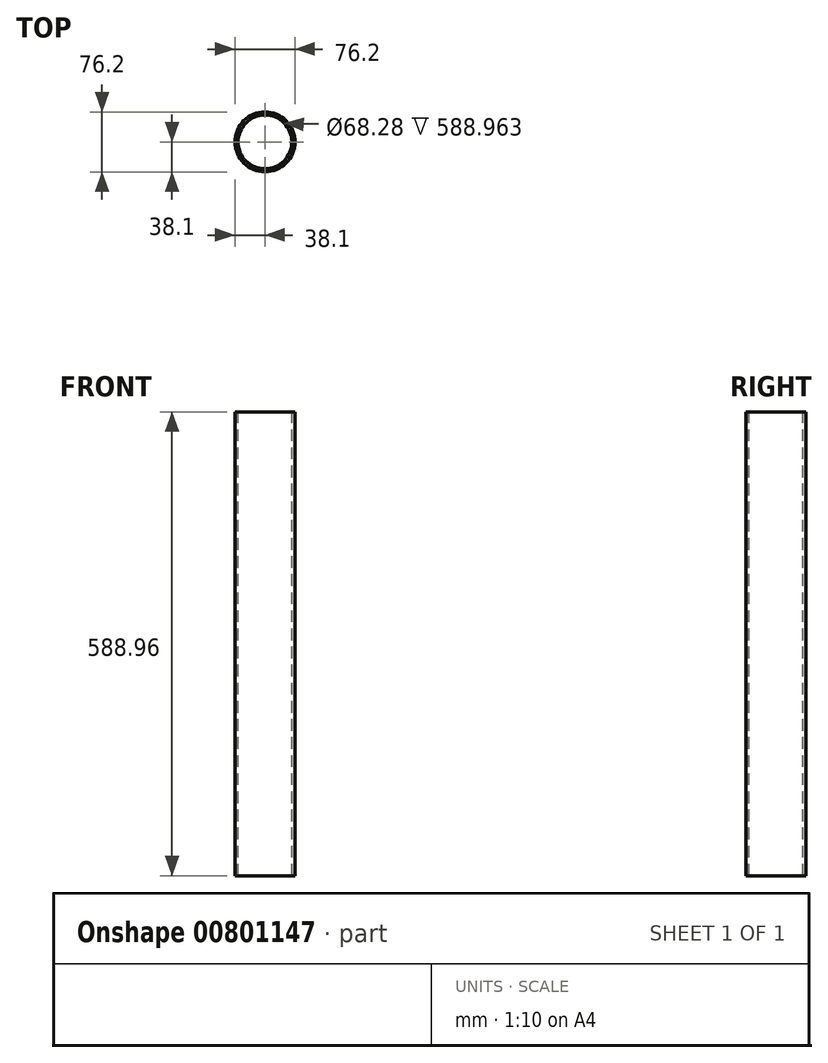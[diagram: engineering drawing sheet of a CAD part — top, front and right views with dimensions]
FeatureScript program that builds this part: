
annotation { "Feature Type Name" : "Feature", "Feature Type Description" : "" }
export const myFeature = defineFeature(function(context is Context, id is Id, definition is map)
    precondition{}
    {
        {
            var Q0;
            Q0=qCreatedBy(makeId("Top.planeOp"),FACE);
            var sketch = newSketch(context, id + "F0", { "sketchPlane" : qUnion([Q0])});
            skCircle(sketch, "E0", {"center": v(0, 0) * mm, "radius": 38.1 * mm});
            skCircle(sketch, "E1", {"center": v(0, 0) * mm, "radius": 34.14 * mm});
            skSolve(sketch);
        }
        {
            var Q0;
            Q0=makeQuery(id+"F0.imprint","IMPRINT",FACE,{"disambiguationData":[TD([[makeQuery(id+"F0.imprint","IMPRINT",EDGE,{"derivedFrom":sQuery(id+"F0.wireOp",EDGE,"E0")}),1.0]])]});
            extrude(context, id + "F1", {"entities" : qUnion([Q0]), "oppositeDirection" : true, "depth" : 588.96 * mm, "offsetDistance" : 25.4 * mm});
        }
        {
            var Q0;
            Q0=makeQuery(id+"F1.opExtrude","CAP_FACE",FACE,{"disambiguationData":[OSD([sQuery(id+"F0.wireOp",EDGE,"E0"),sQuery(id+"F0.wireOp",EDGE,"E1")])],"isStart":false});
            cPlane(context, id + "F2", {"entities" : qUnion([Q0]), "cplaneType" : CPlaneType.OFFSET, "offset" : 4.76 * mm, "oppositeDirection" : true, "width" : 152.4 * mm, "height" : 152.4 * mm});
        }
    });
